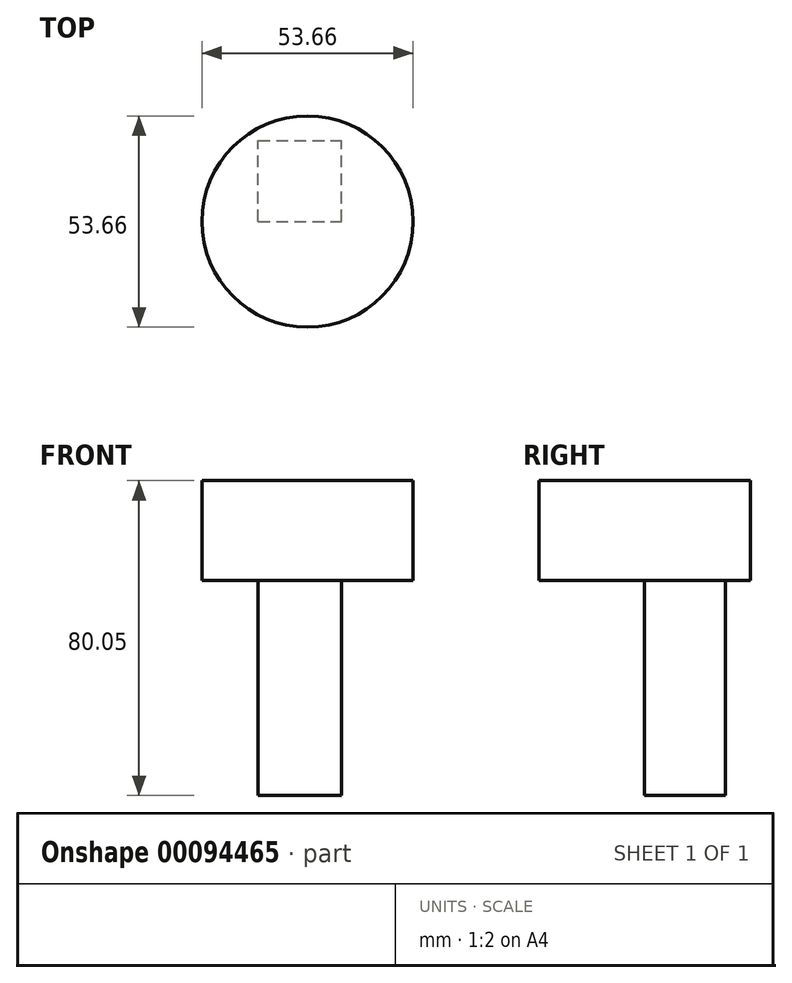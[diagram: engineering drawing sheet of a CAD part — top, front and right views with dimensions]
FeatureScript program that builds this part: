
annotation { "Feature Type Name" : "Feature", "Feature Type Description" : "" }
export const myFeature = defineFeature(function(context is Context, id is Id, definition is map)
    precondition{}
    {
        {
            var Q0;
            Q0=qCreatedBy(makeId("Top.planeOp"),FACE);
            var sketch = newSketch(context, id + "F0", { "sketchPlane" : qUnion([Q0])});
            skCircle(sketch, "E0", {"center": v(0, 0) * mm, "radius": 26.83 * mm});
            skSolve(sketch);
        }
        {
            var Q0;
            Q0=makeQuery(id+"F0.imprint","IMPRINT",FACE,{"disambiguationData":[TD([[makeQuery(id+"F0.imprint","IMPRINT",EDGE,{"derivedFrom":sQuery(id+"F0.wireOp",EDGE,"E0")}),1.0]])]});
            extrude(context, id + "F1", {"entities" : qUnion([Q0]), "depth" : 25.4 * mm});
        }
        {
            var Q0;
            Q0=makeQuery(id+"F1.opExtrude","CAP_FACE",FACE,{"disambiguationData":[OSD([sQuery(id+"F0.wireOp",EDGE,"E0")])],"isStart":false});
            var sketch = newSketch(context, id + "F2", { "sketchPlane" : qUnion([Q0])});
            skLineSegment(sketch, "E1.bottom", {"start": v(-12.52, 0) * mm, "end": v(8.66, 0) * mm});
            skLineSegment(sketch, "E1.top", {"start": v(-12.52, 20.51) * mm, "end": v(8.66, 20.51) * mm});
            skLineSegment(sketch, "E1.left", {"start": v(-12.52, 0) * mm, "end": v(-12.52, 20.51) * mm});
            skLineSegment(sketch, "E1.right", {"start": v(8.66, 0) * mm, "end": v(8.66, 20.51) * mm});
            skSolve(sketch);
        }
        {
            var Q0;
            Q0=makeQuery(id+"F2.imprint","IMPRINT",FACE,{"disambiguationData":[TD([[makeQuery(id+"F2.imprint","IMPRINT",EDGE,{"derivedFrom":sQuery(id+"F2.wireOp",EDGE,"E1.bottom")}),1.0]])]});
            extrude(context, id + "F3", {"entities" : qUnion([Q0]), "operationType" : NewBodyOperationType.ADD, "endBound" : BoundingType.THROUGH_ALL, "oppositeDirection" : true, "depth" : 25.4 * mm});
        }
    });
